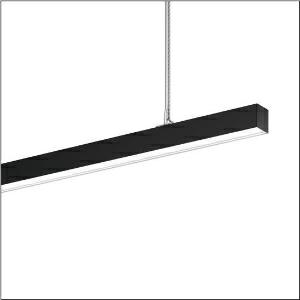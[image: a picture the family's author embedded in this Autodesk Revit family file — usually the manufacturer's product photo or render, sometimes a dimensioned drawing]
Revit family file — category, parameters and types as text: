
# Revit family: silica_r__21_51mx33tctdb_eeca
name_source: partatom
category: Lighting Fixtures
units: mm (PartAtom-declared; Revit-internal decimal feet)

## family parameters
Cut with Voids When Loaded = No
Host = Face
Light Source = No
Part Type = Normal
Room Calculation Point = No
Round Connector Dimension = Use Diameter
Shared = No

## types (1)
- --- (1 x LED, 14340 lm, 134.7 W, 6500K)
    Apparent Load = 135 VA
    CIE Flux Codes = 78 96 99 56 100
    Color Rendering = 80
    Color Temperature = 6500K
    Default Elevation = 1800 mm
    Description = Silica® 21, office luminaire, primary optical cover: prismatic diffuser, of PMMA, CAT 2 (L<= 3000cd/m²), light emission: direct/indirect distribution, primary light characteristic: symmetric, installation type: suspended mounting, LED, rated luminous flux: 14.340lm, luminous efficacy: 101lm/W, light colour: 8tw, colour temperature: 2700..6500K, control gear: ECG DALI, with terminal, 3+2-pole, max. 2.5mm², mains connection: 220..240V, AC, 50/60Hz, rated input power: 141.4W, luminaire housing, of aluminium, jet black (RAL 9005), length: 3.004mm, width: 53mm, height: 53mm, protection rating (complete): IP20, insulation class (complete): insulation class I (protective earthing), certification: CE, permissible operating ambient temperature: 0..+35°C, standard: EN 50419, packaging unit: 1 piece
    Height = 53 mm
    Lamp = 1 x LED
    Lamp Light Flux = 14340 lm
    Lamp Power = 134.7 W
    Lamp count = 1
    Length = 3004 mm
    Luminous efficacy = 106 lm/W
    Manufacturer = Siteco
    ModVariant = No
    Model = 51MX33TCTDB
    Mounting Place = Ceiling
    Mounting Type = Pendant
    Number of Poles = 1
    OnlyDefault = Yes
    Power Factor = 1
    Product Name = Silica® 21
    Product group = office luminaire | ceiling pendant
    ProductGroupID = 902
    Protection Class = Protection class I
    Protection Degree = IP 20
    RLX_Detail_Level = 1
    RLX_Emergency_Light_Flux = 0 lm
    RLX_Emergency_Type = 0
    RLX_Emergency_Type_DB = No
    RlxData = <blob elided: 22849 chars, md5=800a6987>
    Socket = socket
    Standby Power = 0 W
    System Light Flux = 14340 lm
    System Power = 135 W
    Type Comments = individual setting
    Type Image = l_1335856.jpg
    URL = http://relux.com
    VarID = @adj_109555
    Voltage = 0 V
    Weight = 0.00 kg
    Width = 53 mm

## geometry (parser evidence)
native form markers: Blend x4, Sweep x13
no freeform markers — native parametric forms only
